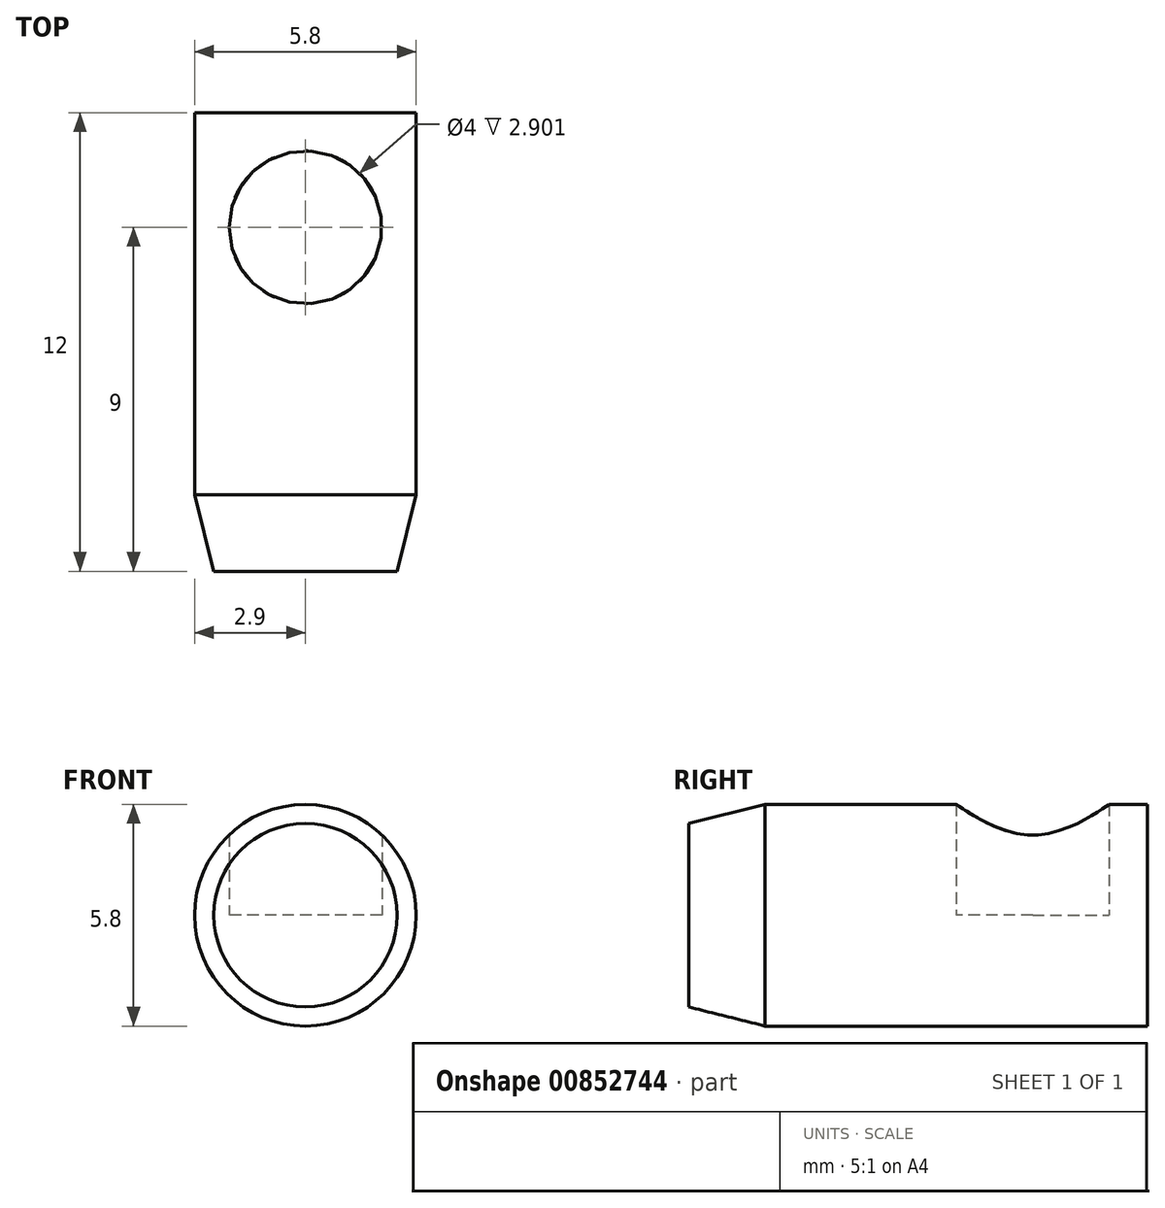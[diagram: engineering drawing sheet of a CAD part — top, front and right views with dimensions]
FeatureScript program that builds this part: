
annotation { "Feature Type Name" : "Feature", "Feature Type Description" : "" }
export const myFeature = defineFeature(function(context is Context, id is Id, definition is map)
    precondition{}
    {
        {
            var Q0;
            Q0=qCreatedBy(makeId("Front.planeOp"),FACE);
            var sketch = newSketch(context, id + "F0", { "sketchPlane" : qUnion([Q0])});
            skPoint(sketch, "E0.middle", {"position": v(0, 0) * mm});
            skCircle(sketch, "E1", {"center": v(0, 0) * mm, "radius": 2.9 * mm});
            skSolve(sketch);
        }
        {
            var Q0;
            Q0=makeQuery(id+"F0.imprint","IMPRINT",FACE,{"disambiguationData":[TD([[makeQuery(id+"F0.imprint","IMPRINT",EDGE,{"derivedFrom":sQuery(id+"F0.wireOp",EDGE,"E1")}),1.0]])]});
            var Q1;
            Q1=sQuery(id+"F0.wireOp",EDGE,"qRAeb4V8-xsSo-21TQ-gvrW-piL1NY28KVn1");
            extrude(context, id + "F1", {"entities" : qUnion([Q0]), "surfaceEntities" : qUnion([Q1]), "endBound" : BoundingType.SYMMETRIC, "depth" : 12 * mm, "offsetDistance" : 25 * mm});
        }
        {
            var Q0;
            Q0=qCreatedBy(makeId("Top.planeOp"),FACE);
            var sketch = newSketch(context, id + "F2", { "sketchPlane" : qUnion([Q0])});
            skPoint(sketch, "E2.middle", {"position": v(0, 0) * mm});
            skCircle(sketch, "E3", {"center": v(0, 3) * mm, "radius": 2 * mm});
            skSolve(sketch);
        }
        {
            var Q0;
            Q0 = qSketchRegion(id + "F2", true);
            extrude(context, id + "F3", {"entities" : qUnion([Q0]), "operationType" : NewBodyOperationType.REMOVE, "endBound" : BoundingType.UP_TO_NEXT, "depth" : 10 * mm, "offsetDistance" : 25 * mm});
        }
        {
            var Q0;
            Q0=makeQuery(id+"F1.opExtrude","CAP_EDGE",EDGE,{"disambiguationData":[OSD([sQuery(id+"F0.wireOp",EDGE,"E1")])],"isStart":false});
            chamfer(context, id + "F4", {"entities" : qUnion([Q0]), "chamferType" : ChamferType.TWO_OFFSETS, "width1" : 0.5 * mm, "oppositeDirection" : false, "width2" : 2 * mm, "tangentPropagation" : true});
        }
    });
